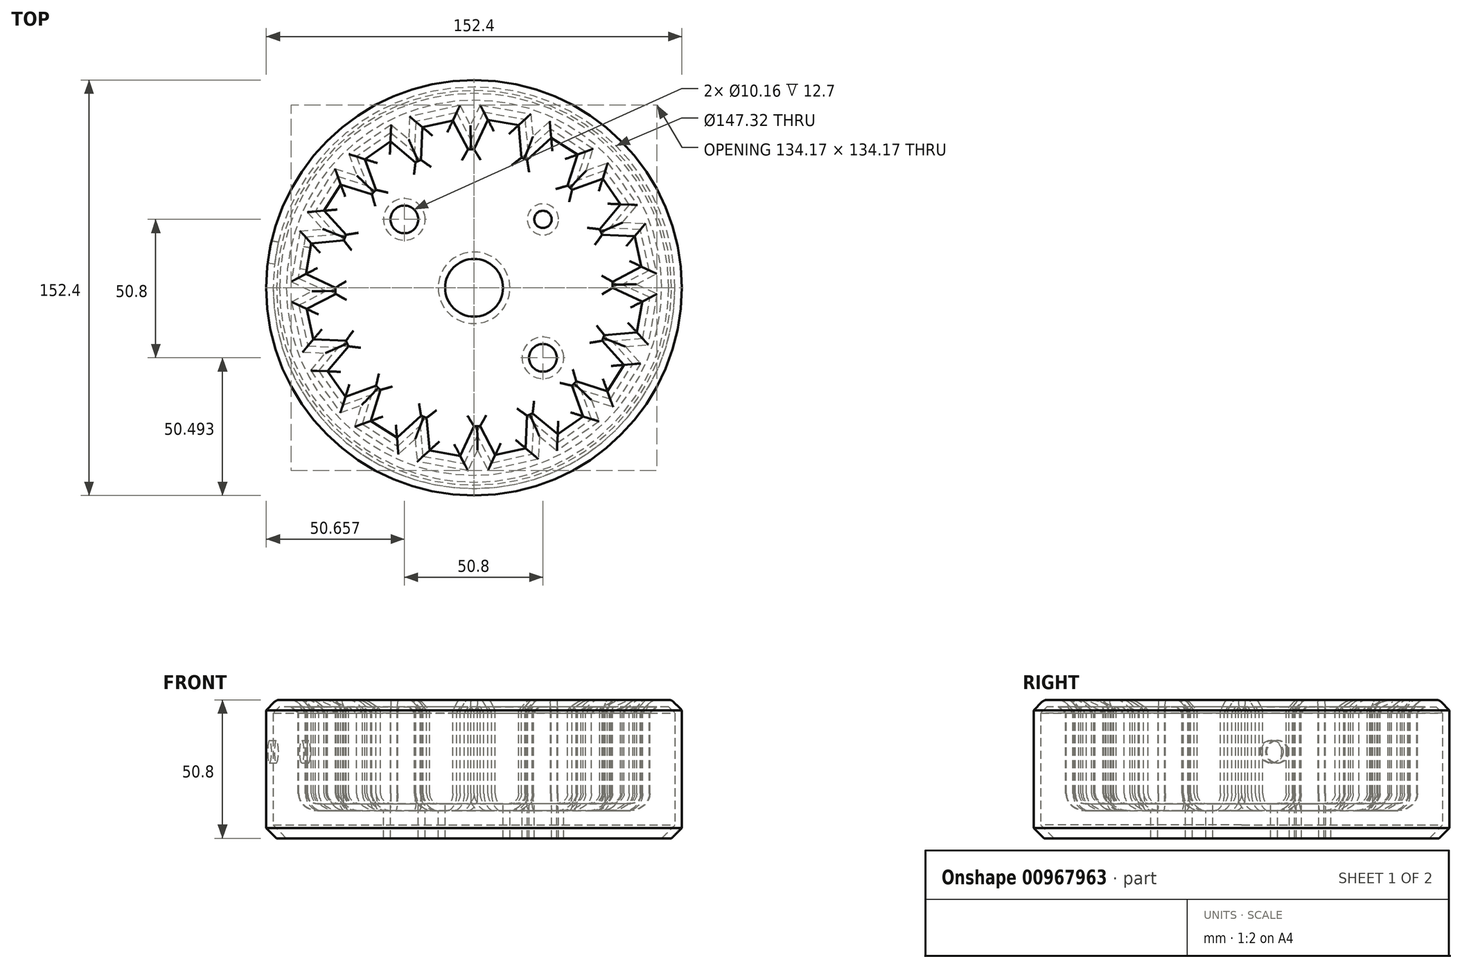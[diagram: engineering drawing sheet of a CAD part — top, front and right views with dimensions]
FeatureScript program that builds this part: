
annotation { "Feature Type Name" : "Feature", "Feature Type Description" : "" }
export const myFeature = defineFeature(function(context is Context, id is Id, definition is map)
    precondition{}
    {
        {
            var Q0;
            Q0=qCreatedBy(makeId("Top.planeOp"),FACE);
            var sketch = newSketch(context, id + "F0", { "sketchPlane" : qUnion([Q0])});
            skCircle(sketch, "E0", {"center": v(0, 0) * mm, "radius": 76.2 * mm});
            skSolve(sketch);
        }
        {
            var Q0;
            Q0=makeQuery(id+"F0.imprint","IMPRINT",FACE,{"disambiguationData":[TD([[makeQuery(id+"F0.imprint","IMPRINT",EDGE,{"derivedFrom":sQuery(id+"F0.wireOp",EDGE,"E0")}),1.0]])]});
            extrude(context, id + "F1", {"entities" : qUnion([Q0]), "depth" : 101.6 * mm, "offsetDistance" : 25.4 * mm});
        }
        {
            var Q0;
            Q0=makeQuery(id+"F1.opExtrude","CAP_FACE",FACE,{"disambiguationData":[OSD([sQuery(id+"F0.wireOp",EDGE,"E0")])],"isStart":false});
            var sketch = newSketch(context, id + "F2", { "sketchPlane" : qUnion([Q0])});
            skCircle(sketch, "E1", {"center": v(0, 0) * mm, "radius": 50.8 * mm});
            skLineSegment(sketch, "E2", {"start": v(10.7, 60.66) * mm, "end": v(5.07, 61.65) * mm});
            skLineSegment(sketch, "E3", {"start": v(10.7, 60.66) * mm, "end": v(16.32, 59.67) * mm});
            skLineSegment(sketch, "E4", {"start": v(16.32, 59.67) * mm, "end": v(17.37, 47.74) * mm});
            skLineSegment(sketch, "E5", {"start": v(5.07, 61.65) * mm, "end": v(0, 50.8) * mm});
            skLineSegment(sketch, "E6.1.0", {"start": v(-7.75, 61.37) * mm, "end": v(-2.22, 50.75) * mm});
            skLineSegment(sketch, "E6.1.1", {"start": v(-18.91, 58.9) * mm, "end": v(-19.44, 46.93) * mm});
            skLineSegment(sketch, "E6.1.2", {"start": v(-13.33, 60.13) * mm, "end": v(-7.75, 61.37) * mm});
            skLineSegment(sketch, "E6.1.3", {"start": v(-13.33, 60.13) * mm, "end": v(-18.91, 58.9) * mm});
            skLineSegment(sketch, "E6.2.0", {"start": v(-30.65, 53.73) * mm, "end": v(-21.47, 46.04) * mm});
            skLineSegment(sketch, "E6.2.1", {"start": v(-40.01, 47.18) * mm, "end": v(-35.92, 35.92) * mm});
            skLineSegment(sketch, "E6.2.2", {"start": v(-35.33, 50.46) * mm, "end": v(-30.65, 53.73) * mm});
            skLineSegment(sketch, "E6.2.3", {"start": v(-35.33, 50.46) * mm, "end": v(-40.01, 47.18) * mm});
            skLineSegment(sketch, "E7.2.3.0", {"start": v(-48.88, 37.91) * mm, "end": v(-37.45, 34.32) * mm});
            skLineSegment(sketch, "E7.3.3.0", {"start": v(-55.02, 28.27) * mm, "end": v(-46.93, 19.44) * mm});
            skLineSegment(sketch, "E7.6.3.0", {"start": v(-51.95, 33.1) * mm, "end": v(-48.88, 37.91) * mm});
            skLineSegment(sketch, "E7.9.3.0", {"start": v(-51.95, 33.1) * mm, "end": v(-55.02, 28.27) * mm});
            skLineSegment(sketch, "E7.2.4.0", {"start": v(-59.67, 16.32) * mm, "end": v(-47.74, 17.37) * mm});
            skLineSegment(sketch, "E7.3.4.0", {"start": v(-61.65, 5.07) * mm, "end": v(-50.8, 0) * mm});
            skLineSegment(sketch, "E7.6.4.0", {"start": v(-60.66, 10.7) * mm, "end": v(-59.67, 16.32) * mm});
            skLineSegment(sketch, "E7.9.4.0", {"start": v(-60.66, 10.7) * mm, "end": v(-61.65, 5.07) * mm});
            skLineSegment(sketch, "E8.2.5.0", {"start": v(-61.37, -7.75) * mm, "end": v(-50.75, -2.22) * mm});
            skLineSegment(sketch, "E8.3.5.0", {"start": v(-58.9, -18.91) * mm, "end": v(-46.93, -19.44) * mm});
            skLineSegment(sketch, "E8.6.5.0", {"start": v(-60.13, -13.33) * mm, "end": v(-61.37, -7.75) * mm});
            skLineSegment(sketch, "E8.9.5.0", {"start": v(-60.13, -13.33) * mm, "end": v(-58.9, -18.91) * mm});
            skLineSegment(sketch, "E8.2.6.0", {"start": v(-53.73, -30.65) * mm, "end": v(-46.04, -21.47) * mm});
            skLineSegment(sketch, "E8.3.6.0", {"start": v(-47.18, -40.01) * mm, "end": v(-35.92, -35.92) * mm});
            skLineSegment(sketch, "E8.6.6.0", {"start": v(-50.46, -35.33) * mm, "end": v(-53.73, -30.65) * mm});
            skLineSegment(sketch, "E8.9.6.0", {"start": v(-50.46, -35.33) * mm, "end": v(-47.18, -40.01) * mm});
            skLineSegment(sketch, "E8.2.7.0", {"start": v(-37.91, -48.88) * mm, "end": v(-34.32, -37.45) * mm});
            skLineSegment(sketch, "E8.3.7.0", {"start": v(-28.27, -55.02) * mm, "end": v(-19.44, -46.93) * mm});
            skLineSegment(sketch, "E8.6.7.0", {"start": v(-33.1, -51.95) * mm, "end": v(-37.91, -48.88) * mm});
            skLineSegment(sketch, "E8.9.7.0", {"start": v(-33.1, -51.95) * mm, "end": v(-28.27, -55.02) * mm});
            skLineSegment(sketch, "E8.2.8.0", {"start": v(-16.32, -59.67) * mm, "end": v(-17.37, -47.74) * mm});
            skLineSegment(sketch, "E8.3.8.0", {"start": v(-5.07, -61.65) * mm, "end": v(0, -50.8) * mm});
            skLineSegment(sketch, "E8.6.8.0", {"start": v(-10.7, -60.66) * mm, "end": v(-16.32, -59.67) * mm});
            skLineSegment(sketch, "E8.9.8.0", {"start": v(-10.7, -60.66) * mm, "end": v(-5.07, -61.65) * mm});
            skLineSegment(sketch, "E8.2.9.0", {"start": v(7.75, -61.37) * mm, "end": v(2.22, -50.75) * mm});
            skLineSegment(sketch, "E8.3.9.0", {"start": v(18.91, -58.9) * mm, "end": v(19.44, -46.93) * mm});
            skLineSegment(sketch, "E8.6.9.0", {"start": v(13.33, -60.13) * mm, "end": v(7.75, -61.37) * mm});
            skLineSegment(sketch, "E8.9.9.0", {"start": v(13.33, -60.13) * mm, "end": v(18.91, -58.9) * mm});
            skLineSegment(sketch, "E8.2.10.0", {"start": v(30.65, -53.73) * mm, "end": v(21.47, -46.04) * mm});
            skLineSegment(sketch, "E8.3.10.0", {"start": v(40.01, -47.18) * mm, "end": v(35.92, -35.92) * mm});
            skLineSegment(sketch, "E8.6.10.0", {"start": v(35.33, -50.46) * mm, "end": v(30.65, -53.73) * mm});
            skLineSegment(sketch, "E8.9.10.0", {"start": v(35.33, -50.46) * mm, "end": v(40.01, -47.18) * mm});
            skLineSegment(sketch, "E8.2.11.0", {"start": v(48.88, -37.91) * mm, "end": v(37.45, -34.32) * mm});
            skLineSegment(sketch, "E8.3.11.0", {"start": v(55.02, -28.27) * mm, "end": v(46.93, -19.44) * mm});
            skLineSegment(sketch, "E8.6.11.0", {"start": v(51.95, -33.1) * mm, "end": v(48.88, -37.91) * mm});
            skLineSegment(sketch, "E8.9.11.0", {"start": v(51.95, -33.1) * mm, "end": v(55.02, -28.27) * mm});
            skLineSegment(sketch, "E9.2.12.0", {"start": v(59.67, -16.32) * mm, "end": v(47.74, -17.37) * mm});
            skLineSegment(sketch, "E9.3.12.0", {"start": v(61.65, -5.07) * mm, "end": v(50.8, 0) * mm});
            skLineSegment(sketch, "E9.6.12.0", {"start": v(60.66, -10.7) * mm, "end": v(59.67, -16.32) * mm});
            skLineSegment(sketch, "E9.9.12.0", {"start": v(60.66, -10.7) * mm, "end": v(61.65, -5.07) * mm});
            skLineSegment(sketch, "E10.2.13.0", {"start": v(61.37, 7.75) * mm, "end": v(50.75, 2.22) * mm});
            skLineSegment(sketch, "E10.3.13.0", {"start": v(58.9, 18.91) * mm, "end": v(46.93, 19.44) * mm});
            skLineSegment(sketch, "E10.6.13.0", {"start": v(60.13, 13.33) * mm, "end": v(61.37, 7.75) * mm});
            skLineSegment(sketch, "E10.9.13.0", {"start": v(60.13, 13.33) * mm, "end": v(58.9, 18.91) * mm});
            skLineSegment(sketch, "E10.2.14.0", {"start": v(53.73, 30.65) * mm, "end": v(46.04, 21.47) * mm});
            skLineSegment(sketch, "E10.3.14.0", {"start": v(47.18, 40.01) * mm, "end": v(35.92, 35.92) * mm});
            skLineSegment(sketch, "E10.6.14.0", {"start": v(50.46, 35.33) * mm, "end": v(53.73, 30.65) * mm});
            skLineSegment(sketch, "E10.9.14.0", {"start": v(50.46, 35.33) * mm, "end": v(47.18, 40.01) * mm});
            skLineSegment(sketch, "E11.2.15.0", {"start": v(37.91, 48.88) * mm, "end": v(34.32, 37.45) * mm});
            skLineSegment(sketch, "E11.3.15.0", {"start": v(28.27, 55.02) * mm, "end": v(19.44, 46.93) * mm});
            skLineSegment(sketch, "E11.6.15.0", {"start": v(33.1, 51.95) * mm, "end": v(37.91, 48.88) * mm});
            skLineSegment(sketch, "E11.9.15.0", {"start": v(33.1, 51.95) * mm, "end": v(28.27, 55.02) * mm});
            skSolve(sketch);
        }
        {
            var Q0;
            Q0=makeQuery(id+"F2.imprint","IMPRINT",FACE,{"disambiguationData":[TD([[makeQuery(id+"F2.imprint","IMPRINT",EDGE,{"derivedFrom":sQuery(id+"F2.wireOp",EDGE,"E2")}),-1.0]])]});
            extrude(context, id + "F3", {"entities" : qUnion([Q0]), "operationType" : NewBodyOperationType.REMOVE, "oppositeDirection" : true, "depth" : 50.8 * mm, "offsetDistance" : 25.4 * mm});
        }
        {
            var Q0;
            Q0=makeQuery(id+"F1.opExtrude","CAP_FACE",FACE,{"disambiguationData":[OSD([sQuery(id+"F0.wireOp",EDGE,"E0")])],"isStart":false});
            extrude(context, id + "F4", {"entities" : qUnion([Q0]), "operationType" : NewBodyOperationType.REMOVE, "oppositeDirection" : true, "depth" : 88.9 * mm, "offsetDistance" : 25.4 * mm});
        }
        {
            var Q0;
            Q0=makeQuery(id+"F3.boolean.opBoolean","COPY",EDGE,{"derivedFrom":makeQuery(id+"F3.opExtrude","CAP_EDGE",EDGE,{"disambiguationData":[OSD([sQuery(id+"F0.wireOp",EDGE,"E0")])],"isStart":false})});
            var Q1;
            Q1=makeQuery(id+"F3.boolean.opBoolean","COPY",FACE,{"derivedFrom":makeQuery(id+"F3.opExtrude","CAP_FACE",FACE,{"disambiguationData":[OSD([sQuery(id+"F0.wireOp",EDGE,"E0"),sQuery(id+"F2.wireOp",EDGE,"E1"),sQuery(id+"F2.wireOp",EDGE,"E2"),sQuery(id+"F2.wireOp",EDGE,"E3"),sQuery(id+"F2.wireOp",EDGE,"E4"),sQuery(id+"F2.wireOp",EDGE,"E5"),sQuery(id+"F2.wireOp",EDGE,"E6.1.0"),sQuery(id+"F2.wireOp",EDGE,"E6.1.1"),sQuery(id+"F2.wireOp",EDGE,"E6.1.2"),sQuery(id+"F2.wireOp",EDGE,"E6.1.3"),sQuery(id+"F2.wireOp",EDGE,"E6.2.0"),sQuery(id+"F2.wireOp",EDGE,"E6.2.1"),sQuery(id+"F2.wireOp",EDGE,"E6.2.2"),sQuery(id+"F2.wireOp",EDGE,"E6.2.3"),sQuery(id+"F2.wireOp",EDGE,"E7.2.3.0"),sQuery(id+"F2.wireOp",EDGE,"E7.3.3.0"),sQuery(id+"F2.wireOp",EDGE,"E7.6.3.0"),sQuery(id+"F2.wireOp",EDGE,"E7.9.3.0"),sQuery(id+"F2.wireOp",EDGE,"E7.2.4.0"),sQuery(id+"F2.wireOp",EDGE,"E7.3.4.0"),sQuery(id+"F2.wireOp",EDGE,"E7.6.4.0"),sQuery(id+"F2.wireOp",EDGE,"E7.9.4.0"),sQuery(id+"F2.wireOp",EDGE,"E8.2.5.0"),sQuery(id+"F2.wireOp",EDGE,"E8.3.5.0"),sQuery(id+"F2.wireOp",EDGE,"E8.6.5.0"),sQuery(id+"F2.wireOp",EDGE,"E8.9.5.0"),sQuery(id+"F2.wireOp",EDGE,"E8.2.6.0"),sQuery(id+"F2.wireOp",EDGE,"E8.3.6.0"),sQuery(id+"F2.wireOp",EDGE,"E8.6.6.0"),sQuery(id+"F2.wireOp",EDGE,"E8.9.6.0"),sQuery(id+"F2.wireOp",EDGE,"E8.2.7.0"),sQuery(id+"F2.wireOp",EDGE,"E8.3.7.0"),sQuery(id+"F2.wireOp",EDGE,"E8.6.7.0"),sQuery(id+"F2.wireOp",EDGE,"E8.9.7.0"),sQuery(id+"F2.wireOp",EDGE,"E8.2.8.0"),sQuery(id+"F2.wireOp",EDGE,"E8.3.8.0"),sQuery(id+"F2.wireOp",EDGE,"E8.6.8.0"),sQuery(id+"F2.wireOp",EDGE,"E8.9.8.0"),sQuery(id+"F2.wireOp",EDGE,"E8.2.9.0"),sQuery(id+"F2.wireOp",EDGE,"E8.3.9.0"),sQuery(id+"F2.wireOp",EDGE,"E8.6.9.0"),sQuery(id+"F2.wireOp",EDGE,"E8.9.9.0"),sQuery(id+"F2.wireOp",EDGE,"E8.2.10.0"),sQuery(id+"F2.wireOp",EDGE,"E8.3.10.0"),sQuery(id+"F2.wireOp",EDGE,"E8.6.10.0"),sQuery(id+"F2.wireOp",EDGE,"E8.9.10.0"),sQuery(id+"F2.wireOp",EDGE,"E8.2.11.0"),sQuery(id+"F2.wireOp",EDGE,"E8.3.11.0"),sQuery(id+"F2.wireOp",EDGE,"E8.6.11.0"),sQuery(id+"F2.wireOp",EDGE,"E8.9.11.0"),sQuery(id+"F2.wireOp",EDGE,"E9.2.12.0"),sQuery(id+"F2.wireOp",EDGE,"E9.3.12.0"),sQuery(id+"F2.wireOp",EDGE,"E9.6.12.0"),sQuery(id+"F2.wireOp",EDGE,"E9.9.12.0"),sQuery(id+"F2.wireOp",EDGE,"E10.2.13.0"),sQuery(id+"F2.wireOp",EDGE,"E10.3.13.0"),sQuery(id+"F2.wireOp",EDGE,"E10.6.13.0"),sQuery(id+"F2.wireOp",EDGE,"E10.9.13.0"),sQuery(id+"F2.wireOp",EDGE,"E10.2.14.0"),sQuery(id+"F2.wireOp",EDGE,"E10.3.14.0"),sQuery(id+"F2.wireOp",EDGE,"E10.6.14.0"),sQuery(id+"F2.wireOp",EDGE,"E10.9.14.0"),sQuery(id+"F2.wireOp",EDGE,"E11.2.15.0"),sQuery(id+"F2.wireOp",EDGE,"E11.3.15.0"),sQuery(id+"F2.wireOp",EDGE,"E11.6.15.0"),sQuery(id+"F2.wireOp",EDGE,"E11.9.15.0")])],"isStart":false})});
            var Q2;
            Q2=makeQuery(id+"F1.opExtrude","CAP_FACE",FACE,{"disambiguationData":[OSD([sQuery(id+"F0.wireOp",EDGE,"E0")])],"isStart":true});
            chamfer(context, id + "F5", {"entities" : qUnion([Q0, Q1, Q2]), "width" : 3.8 * mm, "tangentPropagation" : true});
        }
        {
            var Q0;
            Q0=makeQuery(id+"F4.boolean.opBoolean","COPY",FACE,{"derivedFrom":makeQuery(id+"F4.opExtrude","CAP_FACE",FACE,{"disambiguationData":[OSD([sQuery(id+"F0.wireOp",EDGE,"E0")])],"isStart":false})});
            fillet(context, id + "F6", {"entities" : qUnion([Q0]), "radius" : 3.8 * mm, "tangentPropagation" : true, "allowEdgeOverflow" : false});
        }
        {
            var Q0;
            Q0=makeQuery(id+"F4.boolean.opBoolean","COPY",FACE,{"derivedFrom":makeQuery(id+"F4.opExtrude","CAP_FACE",FACE,{"disambiguationData":[OSD([sQuery(id+"F0.wireOp",EDGE,"E0")])],"isStart":false})});
            var sketch = newSketch(context, id + "F7", { "sketchPlane" : qUnion([Q0])});
            skCircle(sketch, "E12", {"center": v(0, 0) * mm, "radius": 10.6 * mm});
            skCircle(sketch, "E13", {"center": v(25.26, 25.1) * mm, "radius": 3.18 * mm});
            skCircle(sketch, "E14", {"center": v(-25.54, 25.1) * mm, "radius": 5.08 * mm});
            skCircle(sketch, "E15", {"center": v(25.26, -25.7) * mm, "radius": 5.08 * mm});
            skSolve(sketch);
        }
        {
            var Q0;
            Q0=makeQuery(id+"F7.imprint","IMPRINT",FACE,{"disambiguationData":[TD([[makeQuery(id+"F7.imprint","IMPRINT",EDGE,{"derivedFrom":sQuery(id+"F7.wireOp",EDGE,"E12")}),1.0]])]});
            var Q1;
            Q1=makeQuery(id+"F7.imprint","IMPRINT",FACE,{"disambiguationData":[TD([[makeQuery(id+"F7.imprint","IMPRINT",EDGE,{"derivedFrom":sQuery(id+"F7.wireOp",EDGE,"E14")}),1.0]])]});
            var Q2;
            Q2=makeQuery(id+"F7.imprint","IMPRINT",FACE,{"disambiguationData":[TD([[makeQuery(id+"F7.imprint","IMPRINT",EDGE,{"derivedFrom":sQuery(id+"F7.wireOp",EDGE,"E15")}),1.0]])]});
            var Q3;
            Q3=makeQuery(id+"F7.imprint","IMPRINT",FACE,{"disambiguationData":[TD([[makeQuery(id+"F7.imprint","IMPRINT",EDGE,{"derivedFrom":sQuery(id+"F7.wireOp",EDGE,"E13")}),1.0]])]});
            var Q4;
            Q4=sQuery(id+"F7.wireOp",EDGE,"E14");
            var Q5;
            Q5=sQuery(id+"F7.wireOp",EDGE,"E13");
            var Q6;
            Q6=sQuery(id+"F7.wireOp",EDGE,"E12");
            var Q7;
            Q7=sQuery(id+"F7.wireOp",EDGE,"E15");
            extrude(context, id + "F8", {"entities" : qUnion([Q0, Q1, Q2, Q3]), "operationType" : NewBodyOperationType.REMOVE, "surfaceEntities" : qUnion([Q4, Q5, Q6, Q7]), "endBound" : BoundingType.THROUGH_ALL, "oppositeDirection" : true, "depth" : 25.4 * mm, "offsetDistance" : 25.4 * mm});
        }
        {
            var Q0;
            Q0=makeQuery(id+"F3.boolean.opBoolean","COPY",FACE,{"derivedFrom":makeQuery(id+"F3.opExtrude","CAP_FACE",FACE,{"disambiguationData":[OSD([sQuery(id+"F0.wireOp",EDGE,"E0"),sQuery(id+"F2.wireOp",EDGE,"E1"),sQuery(id+"F2.wireOp",EDGE,"E2"),sQuery(id+"F2.wireOp",EDGE,"E3"),sQuery(id+"F2.wireOp",EDGE,"E4"),sQuery(id+"F2.wireOp",EDGE,"E5"),sQuery(id+"F2.wireOp",EDGE,"E6.1.0"),sQuery(id+"F2.wireOp",EDGE,"E6.1.1"),sQuery(id+"F2.wireOp",EDGE,"E6.1.2"),sQuery(id+"F2.wireOp",EDGE,"E6.1.3"),sQuery(id+"F2.wireOp",EDGE,"E6.2.0"),sQuery(id+"F2.wireOp",EDGE,"E6.2.1"),sQuery(id+"F2.wireOp",EDGE,"E6.2.2"),sQuery(id+"F2.wireOp",EDGE,"E6.2.3"),sQuery(id+"F2.wireOp",EDGE,"E7.2.3.0"),sQuery(id+"F2.wireOp",EDGE,"E7.3.3.0"),sQuery(id+"F2.wireOp",EDGE,"E7.6.3.0"),sQuery(id+"F2.wireOp",EDGE,"E7.9.3.0"),sQuery(id+"F2.wireOp",EDGE,"E7.2.4.0"),sQuery(id+"F2.wireOp",EDGE,"E7.3.4.0"),sQuery(id+"F2.wireOp",EDGE,"E7.6.4.0"),sQuery(id+"F2.wireOp",EDGE,"E7.9.4.0"),sQuery(id+"F2.wireOp",EDGE,"E8.2.5.0"),sQuery(id+"F2.wireOp",EDGE,"E8.3.5.0"),sQuery(id+"F2.wireOp",EDGE,"E8.6.5.0"),sQuery(id+"F2.wireOp",EDGE,"E8.9.5.0"),sQuery(id+"F2.wireOp",EDGE,"E8.2.6.0"),sQuery(id+"F2.wireOp",EDGE,"E8.3.6.0"),sQuery(id+"F2.wireOp",EDGE,"E8.6.6.0"),sQuery(id+"F2.wireOp",EDGE,"E8.9.6.0"),sQuery(id+"F2.wireOp",EDGE,"E8.2.7.0"),sQuery(id+"F2.wireOp",EDGE,"E8.3.7.0"),sQuery(id+"F2.wireOp",EDGE,"E8.6.7.0"),sQuery(id+"F2.wireOp",EDGE,"E8.9.7.0"),sQuery(id+"F2.wireOp",EDGE,"E8.2.8.0"),sQuery(id+"F2.wireOp",EDGE,"E8.3.8.0"),sQuery(id+"F2.wireOp",EDGE,"E8.6.8.0"),sQuery(id+"F2.wireOp",EDGE,"E8.9.8.0"),sQuery(id+"F2.wireOp",EDGE,"E8.2.9.0"),sQuery(id+"F2.wireOp",EDGE,"E8.3.9.0"),sQuery(id+"F2.wireOp",EDGE,"E8.6.9.0"),sQuery(id+"F2.wireOp",EDGE,"E8.9.9.0"),sQuery(id+"F2.wireOp",EDGE,"E8.2.10.0"),sQuery(id+"F2.wireOp",EDGE,"E8.3.10.0"),sQuery(id+"F2.wireOp",EDGE,"E8.6.10.0"),sQuery(id+"F2.wireOp",EDGE,"E8.9.10.0"),sQuery(id+"F2.wireOp",EDGE,"E8.2.11.0"),sQuery(id+"F2.wireOp",EDGE,"E8.3.11.0"),sQuery(id+"F2.wireOp",EDGE,"E8.6.11.0"),sQuery(id+"F2.wireOp",EDGE,"E8.9.11.0"),sQuery(id+"F2.wireOp",EDGE,"E9.2.12.0"),sQuery(id+"F2.wireOp",EDGE,"E9.3.12.0"),sQuery(id+"F2.wireOp",EDGE,"E9.6.12.0"),sQuery(id+"F2.wireOp",EDGE,"E9.9.12.0"),sQuery(id+"F2.wireOp",EDGE,"E10.2.13.0"),sQuery(id+"F2.wireOp",EDGE,"E10.3.13.0"),sQuery(id+"F2.wireOp",EDGE,"E10.6.13.0"),sQuery(id+"F2.wireOp",EDGE,"E10.9.13.0"),sQuery(id+"F2.wireOp",EDGE,"E10.2.14.0"),sQuery(id+"F2.wireOp",EDGE,"E10.3.14.0"),sQuery(id+"F2.wireOp",EDGE,"E10.6.14.0"),sQuery(id+"F2.wireOp",EDGE,"E10.9.14.0"),sQuery(id+"F2.wireOp",EDGE,"E11.2.15.0"),sQuery(id+"F2.wireOp",EDGE,"E11.3.15.0"),sQuery(id+"F2.wireOp",EDGE,"E11.6.15.0"),sQuery(id+"F2.wireOp",EDGE,"E11.9.15.0")])],"isStart":false})});
            fillet(context, id + "F9", {"entities" : qUnion([Q0]), "radius" : 2.54 * mm, "tangentPropagation" : true, "allowEdgeOverflow" : false});
        }
        {
            var Q0;
            Q0=makeQuery(id+"F1.opExtrude","CAP_FACE",FACE,{"disambiguationData":[OSD([sQuery(id+"F0.wireOp",EDGE,"E0")])],"isStart":true});
            shell(context, id + "F10", {"entities" : qUnion([Q0]), "thickness" : 2.54 * mm});
        }
        {
            var Q0;
            Q0=makeQuery(id+"F4.boolean.opBoolean","COPY",FACE,{"derivedFrom":makeQuery(id+"F4.opExtrude","SWEPT_FACE",FACE,{"disambiguationData":[OSD([sQuery(id+"F2.wireOp",EDGE,"E7.6.4.0"),sQuery(id+"F2.wireOp",EDGE,"E7.9.4.0")])]})});
            var sketch = newSketch(context, id + "F11", { "sketchPlane" : qUnion([Q0])});
            skCircle(sketch, "E16", {"center": v(0, 31.75) * mm, "radius": 4.11 * mm});
            skSolve(sketch);
        }
        {
            var Q0;
            Q0 = qSketchRegion(id + "F11", true);
            extrude(context, id + "F12", {"entities" : qUnion([Q0]), "operationType" : NewBodyOperationType.REMOVE, "oppositeDirection" : true, "depth" : 25.4 * mm, "offsetDistance" : 25.4 * mm});
        }
    });
